# Revit family: GRAS_HW-52W-15-20 Ko
name_source: partatom
category: Osprzęt hydrauliczny
revit_build: Autodesk Revit 2018 (Build: 20190510_1515(x64)
units: mm (PartAtom-declared; Revit-internal decimal feet)

## family parameters
Obiekt nadrzędny = Powierzchnia
Punkt obliczania pomieszczeń = Nie
Tnij formami wycięć po wczytaniu = Nie
Typ części = Normalny
Współdzielony = Nie
Wymiar okrągłego złącza = Użyj średnicy

## types (2) — shared parameters
Cabinet_Depth = 180 mm  [stored 0.590551 ft]
Cabinet_Height = 490 mm  [stored 1.60761 ft]
Cabinet_Width = 380 mm  [stored 1.24672 ft]
D1 = 100 mm  [stored 0.328084 ft]
DN = 52 mm
Flow = 246.0 L/s
H1 = 80 mm  [stored 0.262467 ft]
Hole_Depth = 190 mm  [stored 0.62336 ft]
Hole_Height = 510 mm  [stored 1.67323 ft]
Hole_Width = 400 mm  [stored 1.31234 ft]
K_factor = 42
Producent = GRAS PPPH
URL = http://www.gras.pl
W1 = 100 mm  [stored 0.328084 ft]
picH = 60 mm  [stored 0.19685 ft]
zero-valued in all types: Domyślna rzędna, zer0

## per-type parameters (varying)
| type | Cabinet_Material | Opis |
| HW-52W-15-20 Ko, RAL9010 | DC01, RAL9010 |  |
| HW-52W-15-20 Ko, RAL3000 | DC01, RAL3000 | http://gras.pl |

note: column(s) folded — value = type name in every type: Model

note: [stored X ft] marks values corroborated as IEEE doubles in the binary element streams (Revit-internal decimal feet)

## geometry (parser evidence)
native form markers: Blend x8
no freeform markers — native parametric forms only
